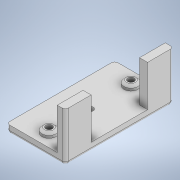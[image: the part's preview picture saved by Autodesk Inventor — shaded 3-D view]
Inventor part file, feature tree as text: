
AUTODESK INVENTOR PART (.ipt)
format: ipt  version: 2022 (Build 260153000, 153)  size: 217,088 bytes
history: native  units: in
note: dims shown in document units (in); Inventor stores cm internally (conversion verified against a paired STEP export)
features: extrude x7, sketch x7, fillet x2, chamfer x1
ambient origin geometry x8: Origin, YZ Plane, XZ Plane, XY Plane, X Axis, Y Axis, Z Axis, Center Point
bodies: Solid1 (feature_tree)
feature tree (17):
  extrude  "Extrusion1"  Depth=2.6378in
  extrude  "Extrusion2"  Depth=0.1969in
  fillet  "Fillet2"  Radius=0.8268in
  extrude  "Extrusion6"  Depth=1.0in
  fillet  "Fillet3"  Radius=1.0in
  extrude  "Extrusion8"  Depth=0.1969in
  chamfer  "Chamfer1"  Distance=1.0in
  extrude  "Extrusion9"  Depth=0.0787in
  extrude  "Extrusion10"  Depth=0.0197in
  extrude  "Extrusion11"  Depth=0.1181in TaperAngle=0.0deg
  sketch  "Sketch1"  dims[d0=1.4331in d1=2.6378in]
  sketch  "Sketch2"  dims[d2=0.1969in d3=0.0in d4=0.1969in d5=0.8268in]
  sketch  "Sketch6"  dims[d6=0.1969in d7=0.8268in d8=1.0in d9=0.0in]
  sketch  "Sketch8"  dims[d25=0.0787in d26=0.1969in]
  sketch  "Sketch9"  dims[d27=0.9449in d28=1.0in d29=0.0in]
  sketch  "Sketch10"  dims[d36=0.0787in d37=0.3406in]
  sketch  "Sketch11"  dims[d38=0.3406in d39=0.3406in d40=0.1181in d41=0.0in d42=0.0591in d43=0.0787in d44=45.0deg d45=0.1575in d46=0.1575in d47=0.1575in d48=0.7874in d49=0.0in d50=0.2362in d51=0.2362in d52=0.2362in d53=0.0984in d54=0.0in d55=1.378in d56=1.9685in d57=0.0in d10=0.0197in d11=0.0344in d13=0.0197in d14=0.0344in d15=0.0197in d16=0.0344in]
